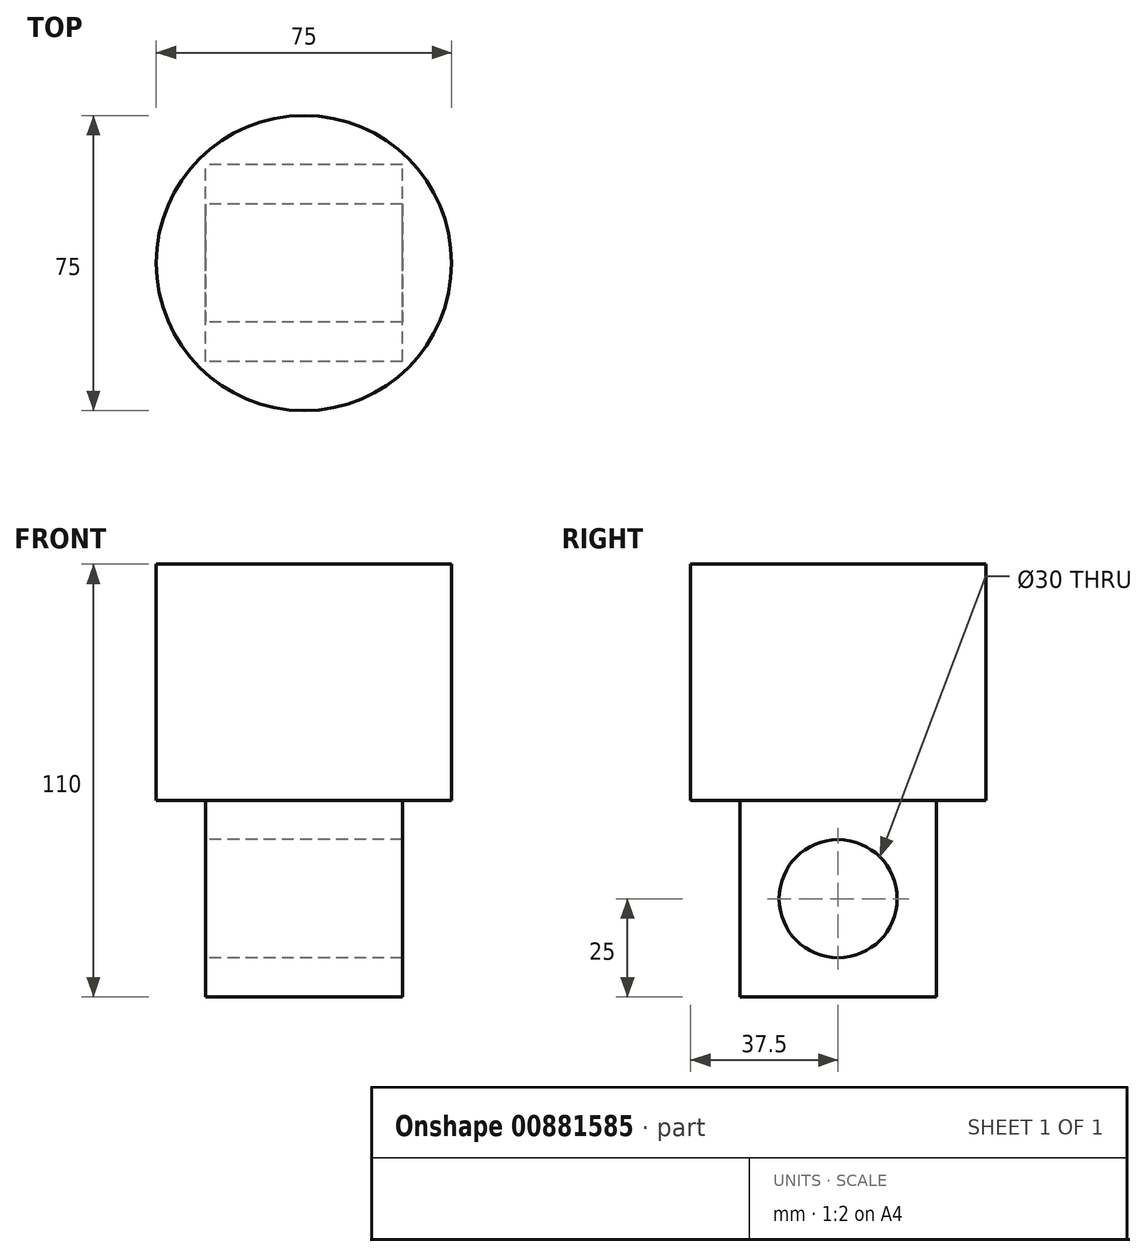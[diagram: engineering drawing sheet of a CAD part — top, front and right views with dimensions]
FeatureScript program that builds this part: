
annotation { "Feature Type Name" : "Feature", "Feature Type Description" : "" }
export const myFeature = defineFeature(function(context is Context, id is Id, definition is map)
    precondition{}
    {
        {
            var Q0;
            Q0=qCreatedBy(makeId("Top.planeOp"),FACE);
            var sketch = newSketch(context, id + "F0", { "sketchPlane" : qUnion([Q0])});
            skCircle(sketch, "E0", {"center": v(0, 0) * mm, "radius": 37.5 * mm});
            skSolve(sketch);
        }
        {
            var Q0;
            Q0 = qSketchRegion(id + "F0", true);
            extrude(context, id + "F1", {"entities" : qUnion([Q0]), "depth" : 60 * mm, "offsetDistance" : 25 * mm});
        }
        {
            var Q0;
            Q0=qCreatedBy(makeId("Right.planeOp"),FACE);
            var sketch = newSketch(context, id + "F2", { "sketchPlane" : qUnion([Q0])});
            skLineSegment(sketch, "E1", {"start": v(0, 0) * mm, "end": v(0, -25) * mm});
            skLineSegment(sketch, "E2.bottom", {"start": v(-25, -50) * mm, "end": v(25, -50) * mm});
            skLineSegment(sketch, "E2.top", {"start": v(-25, 0) * mm, "end": v(25, 0) * mm});
            skLineSegment(sketch, "E2.left", {"start": v(-25, -50) * mm, "end": v(-25, 0) * mm});
            skLineSegment(sketch, "E2.right", {"start": v(25, -50) * mm, "end": v(25, 0) * mm});
            skPoint(sketch, "E2.middle", {"position": v(0, -25) * mm});
            skCircle(sketch, "E3", {"center": v(0, -25) * mm, "radius": 15 * mm});
            skSolve(sketch);
        }
        {
            var Q0;
            Q0 = qSketchRegion(id + "F2", true);
            extrude(context, id + "F3", {"entities" : qUnion([Q0]), "operationType" : NewBodyOperationType.ADD, "depth" : 25 * mm, "offsetDistance" : 25 * mm, "hasSecondDirection" : true, "secondDirectionOppositeDirection" : true, "secondDirectionDepth" : 25 * mm});
        }
    });
